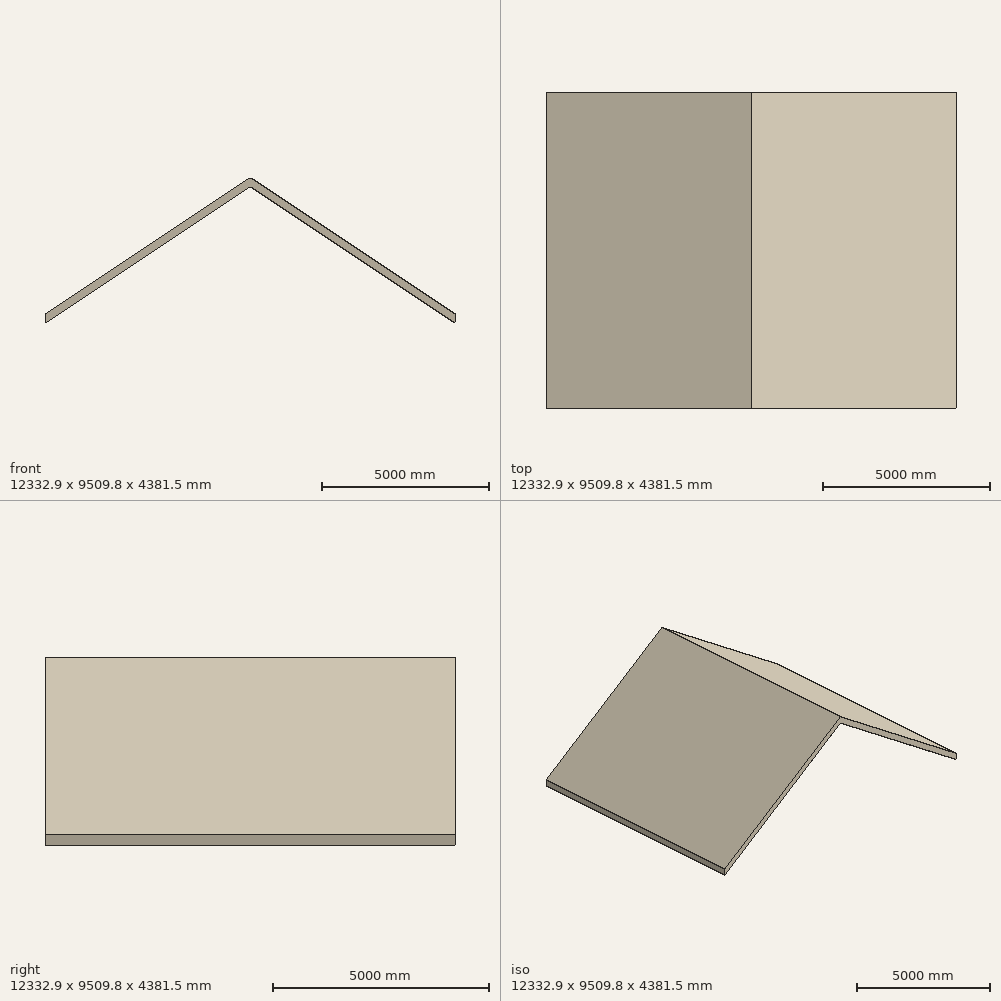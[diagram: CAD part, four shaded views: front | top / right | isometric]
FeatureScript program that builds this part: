
annotation { "Feature Type Name" : "Feature", "Feature Type Description" : "" }
export const myFeature = defineFeature(function(context is Context, id is Id, definition is map)
    precondition{}
    {
        {
            var Q0;
            Q0=qCreatedBy(makeId("Front.planeOp"),FACE);
            var sketch = newSketch(context, id + "F0", { "sketchPlane" : qUnion([Q0])});
            skLineSegment(sketch, "E0.bottom", {"start": v(-5486.4, -2293.96) * mm, "end": v(5486.4, -2293.96) * mm});
            skLineSegment(sketch, "E1", {"start": v(0, -2293.96) * mm, "end": v(0, 4106.84) * mm, "construction": true});
            skLineSegment(sketch, "E2", {"start": v(0, 3903.84) * mm, "end": v(304.8, 3903.84) * mm, "construction": true});
            skLineSegment(sketch, "E3", {"start": v(0, 3903.84) * mm, "end": v(-304.8, 3903.84) * mm, "construction": true});
            skLineSegment(sketch, "E4", {"start": v(0, 4106.84) * mm, "end": v(6166.43, 0) * mm});
            skLineSegment(sketch, "E5", {"start": v(0, 4106.84) * mm, "end": v(-6166.43, 0) * mm});
            skLineSegment(sketch, "E6.bottom", {"start": v(-914.4, 2582.84) * mm, "end": v(914.4, 2582.84) * mm, "construction": true});
            skLineSegment(sketch, "E6.top", {"start": v(-914.4, 1363.64) * mm, "end": v(914.4, 1363.64) * mm, "construction": true});
            skLineSegment(sketch, "E6.left", {"start": v(-914.4, 2582.84) * mm, "end": v(-914.4, 1363.64) * mm, "construction": true});
            skLineSegment(sketch, "E6.right", {"start": v(914.4, 2582.84) * mm, "end": v(914.4, 1363.64) * mm, "construction": true});
            skLineSegment(sketch, "E7", {"start": v(-6166.43, 0) * mm, "end": v(-6166.43, -274.66) * mm});
            skLineSegment(sketch, "E8", {"start": v(-6166.43, -274.66) * mm, "end": v(0, 3832.18) * mm});
            skLineSegment(sketch, "E9", {"start": v(0, 3832.18) * mm, "end": v(6166.43, -274.66) * mm});
            skLineSegment(sketch, "E10", {"start": v(6166.43, -274.66) * mm, "end": v(6166.43, 0) * mm});
            skLineSegment(sketch, "E11", {"start": v(-5486.4, -2293.96) * mm, "end": v(-5486.4, -2751.16) * mm});
            skLineSegment(sketch, "E12", {"start": v(-5486.4, -2751.16) * mm, "end": v(5486.4, -2751.16) * mm});
            skLineSegment(sketch, "E13", {"start": v(5486.4, -2751.16) * mm, "end": v(5486.4, -2293.96) * mm});
            skSolve(sketch);
        }
        {
            var Q0;
            Q0=makeQuery(id+"F0.imprint","IMPRINT",FACE,{"disambiguationData":[TD([[makeQuery(id+"F0.imprint","IMPRINT",EDGE,{"derivedFrom":sQuery(id+"F0.wireOp",EDGE,"E4")}),-1.0]])]});
            extrude(context, id + "F1", {"entities" : qUnion([Q0]), "depth" : 4754.88 * mm, "hasSecondDirection" : true, "secondDirectionOppositeDirection" : true, "secondDirectionDepth" : 4754.88 * mm});
        }
    });
